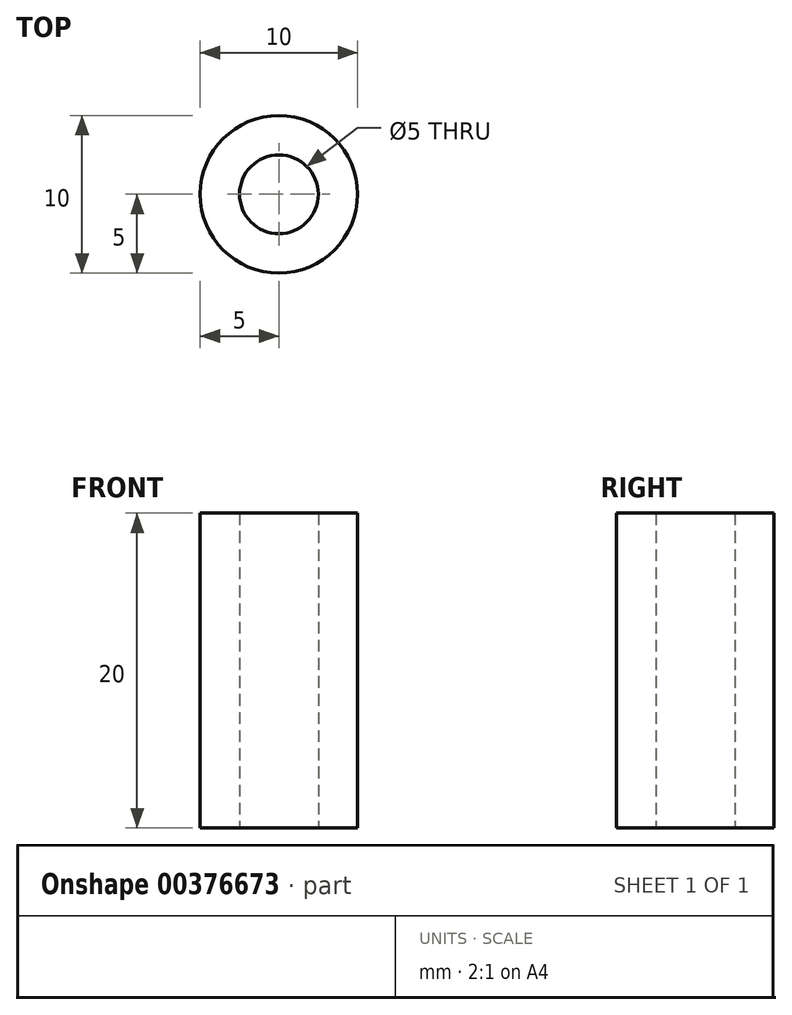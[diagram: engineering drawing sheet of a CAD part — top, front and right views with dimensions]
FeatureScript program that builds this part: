
annotation { "Feature Type Name" : "Feature", "Feature Type Description" : "" }
export const myFeature = defineFeature(function(context is Context, id is Id, definition is map)
    precondition{}
    {
        {
            var Q0;
            Q0=qCreatedBy(makeId("Top.planeOp"),FACE);
            var sketch = newSketch(context, id + "F0", { "sketchPlane" : qUnion([Q0])});
            skCircle(sketch, "E0", {"center": v(0, 0) * mm, "radius": 5 * mm});
            skCircle(sketch, "E1", {"center": v(0, 0) * mm, "radius": 2.5 * mm});
            skSolve(sketch);
        }
        {
            var Q0;
            Q0=makeQuery(id+"F0.imprint","IMPRINT",FACE,{"disambiguationData":[TD([[makeQuery(id+"F0.imprint","IMPRINT",EDGE,{"derivedFrom":sQuery(id+"F0.wireOp",EDGE,"E0")}),1.0]])]});
            extrude(context, id + "F1", {"entities" : qUnion([Q0]), "depth" : 20 * mm, "offsetDistance" : 25 * mm});
        }
    });
